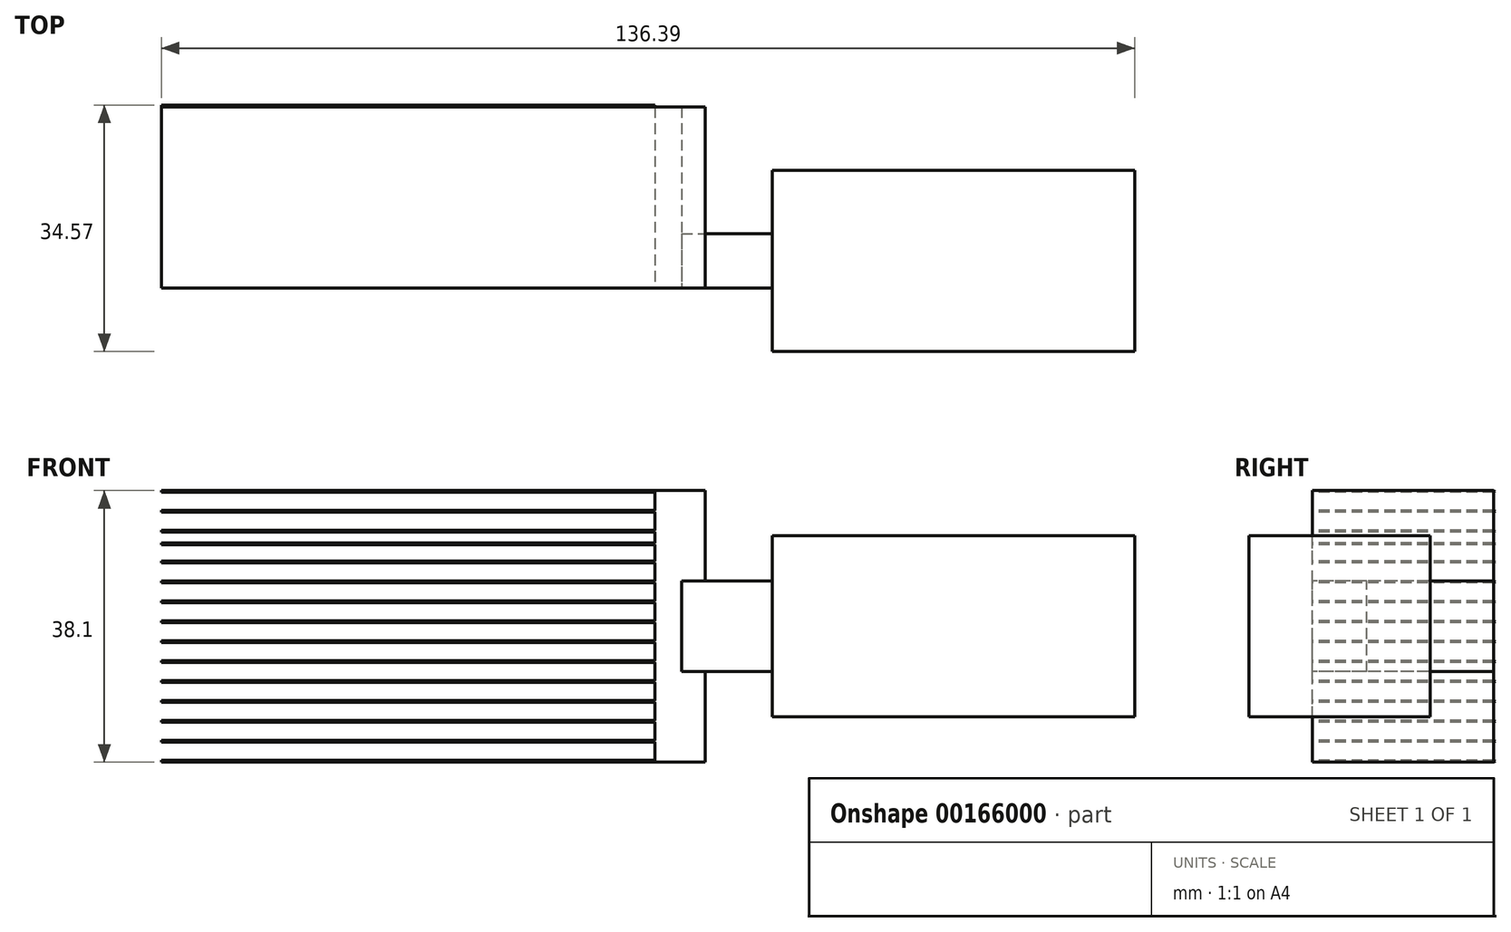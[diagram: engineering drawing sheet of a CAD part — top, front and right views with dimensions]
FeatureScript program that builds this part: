
annotation { "Feature Type Name" : "Feature", "Feature Type Description" : "" }
export const myFeature = defineFeature(function(context is Context, id is Id, definition is map)
    precondition{}
    {
        {
            var Q0;
            Q0=qCreatedBy(makeId("Front.planeOp"),FACE);
            var sketch = newSketch(context, id + "F0", { "sketchPlane" : qUnion([Q0])});
            skLineSegment(sketch, "E0.bottom", {"start": v(0, 0) * mm, "end": v(50.8, 0) * mm});
            skLineSegment(sketch, "E0.top", {"start": v(0, 25.4) * mm, "end": v(50.8, 25.4) * mm});
            skLineSegment(sketch, "E0.left", {"start": v(0, 0) * mm, "end": v(0, 25.4) * mm});
            skLineSegment(sketch, "E0.right", {"start": v(50.8, 0) * mm, "end": v(50.8, 25.4) * mm});
            skSolve(sketch);
        }
        {
            var Q0;
            Q0=makeQuery(id+"F0.imprint","IMPRINT",FACE,{"disambiguationData":[TD([[makeQuery(id+"F0.imprint","IMPRINT",EDGE,{"derivedFrom":sQuery(id+"F0.wireOp",EDGE,"E0.bottom")}),1.0]])]});
            extrude(context, id + "F1", {"entities" : qUnion([Q0]), "depth" : 25.4 * mm});
        }
        {
            var Q0;
            Q0=makeQuery(id+"F1.opExtrude","SWEPT_FACE",FACE,{"disambiguationData":[OSD([sQuery(id+"F0.wireOp",EDGE,"E0.left")])]});
            var sketch = newSketch(context, id + "F2", { "sketchPlane" : qUnion([Q0])});
            skLineSegment(sketch, "E1.0", {"start": v(8.9, 6.35) * mm, "end": v(16.51, 6.35) * mm});
            skLineSegment(sketch, "E2.0", {"start": v(8.9, 19.05) * mm, "end": v(16.51, 19.05) * mm});
            skLineSegment(sketch, "E3.0", {"start": v(16.51, 6.35) * mm, "end": v(16.51, 19.05) * mm});
            skLineSegment(sketch, "E4.0", {"start": v(8.9, 6.35) * mm, "end": v(8.9, 19.05) * mm});
            skPoint(sketch, "E5.orphan", {"position": v(0, 12.7) * mm});
            skPoint(sketch, "E6.orphan", {"position": v(12.7, 25.4) * mm});
            skPoint(sketch, "E7.orphan", {"position": v(25.4, 12.7) * mm});
            skPoint(sketch, "E8.orphan", {"position": v(12.7, 0) * mm});
            skSolve(sketch);
        }
        {
            var Q0;
            Q0 = qSketchRegion(id + "F2", true);
            extrude(context, id + "F3", {"entities" : qUnion([Q0]), "operationType" : NewBodyOperationType.ADD, "depth" : 12.7 * mm});
        }
        {
            var Q0;
            Q0=makeQuery(id+"F3.opExtrude","SWEPT_FACE",FACE,{"disambiguationData":[OSD([sQuery(id+"F2.wireOp",EDGE,"E3.0")])]});
            var sketch = newSketch(context, id + "F4", { "sketchPlane" : qUnion([Q0])});
            skLineSegment(sketch, "E9", {"start": v(-9.39, -6.35) * mm, "end": v(-9.39, 6.35) * mm});
            skLineSegment(sketch, "E10", {"start": v(-9.39, 19.05) * mm, "end": v(-12.7, 19.05) * mm});
            skLineSegment(sketch, "E11", {"start": v(-12.7, 19.05) * mm, "end": v(-12.7, 6.35) * mm});
            skLineSegment(sketch, "E12", {"start": v(-12.7, 6.35) * mm, "end": v(-9.39, 6.35) * mm});
            skLineSegment(sketch, "E13", {"start": v(-9.39, 19.05) * mm, "end": v(-9.39, 31.75) * mm});
            skLineSegment(sketch, "E14", {"start": v(-16.46, 31.75) * mm, "end": v(-85.59, 31.75) * mm});
            skLineSegment(sketch, "E15", {"start": v(-9.39, -6.35) * mm, "end": v(-85.59, -6.35) * mm});
            skLineSegment(sketch, "E16", {"start": v(-85.59, -6.35) * mm, "end": v(-85.59, -6.1) * mm});
            skLineSegment(sketch, "E17", {"start": v(-85.59, -6.1) * mm, "end": v(-16.46, -6.1) * mm});
            skLineSegment(sketch, "E18.0", {"start": v(-85.59, -3.56) * mm, "end": v(-16.46, -3.56) * mm});
            skLineSegment(sketch, "E19.0", {"start": v(-85.59, -3.3) * mm, "end": v(-16.46, -3.3) * mm});
            skLineSegment(sketch, "E20.0", {"start": v(-85.59, -0.76) * mm, "end": v(-16.46, -0.76) * mm});
            skLineSegment(sketch, "E21.0", {"start": v(-16.46, 31.5) * mm, "end": v(-85.59, 31.5) * mm});
            skLineSegment(sketch, "E22.0", {"start": v(-16.46, 28.96) * mm, "end": v(-85.59, 28.96) * mm});
            skLineSegment(sketch, "E23.0", {"start": v(-16.46, 28.7) * mm, "end": v(-85.59, 28.7) * mm});
            skLineSegment(sketch, "E24.0", {"start": v(-16.46, 26.16) * mm, "end": v(-85.59, 26.16) * mm});
            skLineSegment(sketch, "E25.0", {"start": v(-16.46, 25.9) * mm, "end": v(-85.59, 25.9) * mm});
            skLineSegment(sketch, "E26.0", {"start": v(-85.59, -0.5) * mm, "end": v(-16.46, -0.5) * mm});
            skLineSegment(sketch, "E27.0", {"start": v(-85.59, 2.03) * mm, "end": v(-16.46, 2.03) * mm});
            skLineSegment(sketch, "E28.0", {"start": v(-85.59, 2.29) * mm, "end": v(-16.46, 2.29) * mm});
            skLineSegment(sketch, "E29.0", {"start": v(-85.59, 4.83) * mm, "end": v(-16.46, 4.83) * mm});
            skLineSegment(sketch, "E30.0", {"start": v(-85.59, 5.08) * mm, "end": v(-16.46, 5.08) * mm});
            skLineSegment(sketch, "E31.0", {"start": v(-85.59, 7.62) * mm, "end": v(-16.46, 7.62) * mm});
            skLineSegment(sketch, "E32.0", {"start": v(-85.59, 7.87) * mm, "end": v(-16.46, 7.87) * mm});
            skLineSegment(sketch, "E33.0", {"start": v(-85.59, 10.41) * mm, "end": v(-16.46, 10.41) * mm});
            skLineSegment(sketch, "E34.0", {"start": v(-85.59, 10.67) * mm, "end": v(-16.46, 10.67) * mm});
            skLineSegment(sketch, "E35.0", {"start": v(-85.59, 13.2) * mm, "end": v(-16.46, 13.2) * mm});
            skLineSegment(sketch, "E36.0", {"start": v(-85.59, 13.46) * mm, "end": v(-16.46, 13.46) * mm});
            skLineSegment(sketch, "E37.0", {"start": v(-85.59, 16) * mm, "end": v(-16.46, 16) * mm});
            skLineSegment(sketch, "E38.0", {"start": v(-85.59, 16.26) * mm, "end": v(-16.46, 16.26) * mm});
            skLineSegment(sketch, "E39.0", {"start": v(-85.59, 18.8) * mm, "end": v(-16.46, 18.8) * mm});
            skLineSegment(sketch, "E40.0", {"start": v(-85.59, 19.05) * mm, "end": v(-16.46, 19.05) * mm});
            skLineSegment(sketch, "E41.0", {"start": v(-85.59, 21.59) * mm, "end": v(-16.46, 21.59) * mm});
            skLineSegment(sketch, "E42.0", {"start": v(-85.59, 21.84) * mm, "end": v(-16.46, 21.84) * mm});
            skLineSegment(sketch, "E43.0", {"start": v(-85.59, 24.38) * mm, "end": v(-16.46, 24.38) * mm});
            skLineSegment(sketch, "E44.0", {"start": v(-85.59, 24.13) * mm, "end": v(-16.46, 24.13) * mm});
            skLineSegment(sketch, "E45", {"start": v(-16.46, 31.75) * mm, "end": v(-9.39, 31.75) * mm});
            skLineSegment(sketch, "E46", {"start": v(-16.46, -6.1) * mm, "end": v(-16.46, -3.56) * mm});
            skLineSegment(sketch, "E47.trimOffspring", {"start": v(-16.46, 21.84) * mm, "end": v(-16.46, 24.13) * mm});
            skLineSegment(sketch, "E48.trimOffspring", {"start": v(-16.46, 19.05) * mm, "end": v(-16.46, 21.59) * mm});
            skLineSegment(sketch, "E49.trimOffspring", {"start": v(-16.46, 16.26) * mm, "end": v(-16.46, 18.8) * mm});
            skLineSegment(sketch, "E50.trimOffspring", {"start": v(-16.46, 13.46) * mm, "end": v(-16.46, 16) * mm});
            skLineSegment(sketch, "E51.trimOffspring", {"start": v(-16.46, 10.67) * mm, "end": v(-16.46, 13.2) * mm});
            skLineSegment(sketch, "E52.trimOffspring", {"start": v(-16.46, 7.87) * mm, "end": v(-16.46, 10.41) * mm});
            skLineSegment(sketch, "E53.trimOffspring", {"start": v(-16.46, 5.08) * mm, "end": v(-16.46, 7.62) * mm});
            skLineSegment(sketch, "E54.trimOffspring", {"start": v(-16.46, 2.29) * mm, "end": v(-16.46, 4.83) * mm});
            skLineSegment(sketch, "E55.trimOffspring", {"start": v(-16.46, -0.5) * mm, "end": v(-16.46, 2.03) * mm});
            skLineSegment(sketch, "E56.trimOffspring", {"start": v(-16.46, -3.3) * mm, "end": v(-16.46, -0.76) * mm});
            skPoint(sketch, "E57.orphan", {"position": v(-16.46, -6.35) * mm});
            skLineSegment(sketch, "E58", {"start": v(-85.59, -3.56) * mm, "end": v(-85.59, -3.3) * mm});
            skLineSegment(sketch, "E59.trimOffspring", {"start": v(-85.59, 31.5) * mm, "end": v(-85.59, 31.75) * mm});
            skLineSegment(sketch, "E60.trimOffspring", {"start": v(-85.59, 28.7) * mm, "end": v(-85.59, 28.96) * mm});
            skLineSegment(sketch, "E61.trimOffspring", {"start": v(-85.59, 25.9) * mm, "end": v(-85.59, 26.16) * mm});
            skLineSegment(sketch, "E62.trimOffspring", {"start": v(-85.59, 24.13) * mm, "end": v(-85.59, 24.38) * mm});
            skLineSegment(sketch, "E63.trimOffspring", {"start": v(-85.59, 21.59) * mm, "end": v(-85.59, 21.84) * mm});
            skLineSegment(sketch, "E64.trimOffspring", {"start": v(-85.59, 18.8) * mm, "end": v(-85.59, 19.05) * mm});
            skLineSegment(sketch, "E65.trimOffspring", {"start": v(-85.59, 16) * mm, "end": v(-85.59, 16.26) * mm});
            skLineSegment(sketch, "E66.trimOffspring", {"start": v(-85.59, 13.2) * mm, "end": v(-85.59, 13.46) * mm});
            skLineSegment(sketch, "E67.trimOffspring", {"start": v(-85.59, 10.41) * mm, "end": v(-85.59, 10.67) * mm});
            skLineSegment(sketch, "E68.trimOffspring", {"start": v(-85.59, 7.62) * mm, "end": v(-85.59, 7.87) * mm});
            skLineSegment(sketch, "E69.trimOffspring", {"start": v(-85.59, 4.83) * mm, "end": v(-85.59, 5.08) * mm});
            skLineSegment(sketch, "E70.trimOffspring", {"start": v(-85.59, 2.03) * mm, "end": v(-85.59, 2.29) * mm});
            skLineSegment(sketch, "E71.trimOffspring", {"start": v(-85.59, -0.76) * mm, "end": v(-85.59, -0.5) * mm});
            skLineSegment(sketch, "E72", {"start": v(-16.46, 24.38) * mm, "end": v(-16.46, 25.9) * mm});
            skLineSegment(sketch, "E73", {"start": v(-16.46, 26.16) * mm, "end": v(-16.46, 28.7) * mm});
            skLineSegment(sketch, "E74", {"start": v(-16.46, 28.96) * mm, "end": v(-16.46, 31.5) * mm});
            skSolve(sketch);
        }
        {
            var Q0;
            Q0 = qSketchRegion(id + "F4", true);
            extrude(context, id + "F5", {"entities" : qUnion([Q0]), "oppositeDirection" : true, "depth" : 25.4 * mm});
        }
        {
            var Q0;
            Q0=makeQuery(id+"F5.opExtrude","SWEPT_FACE",FACE,{"disambiguationData":[OSD([sQuery(id+"F4.wireOp",EDGE,"E59.trimOffspring")])]});
            var sketch = newSketch(context, id + "F6", { "sketchPlane" : qUnion([Q0])});
            skLineSegment(sketch, "E75", {"start": v(-8.89, 31.75) * mm, "end": v(-9.11, 31.62) * mm});
            skPoint(sketch, "E75.endSnap0", {"position": v(-8.89, 31.62) * mm});
            skLineSegment(sketch, "E76", {"start": v(-9.11, 31.62) * mm, "end": v(-8.89, 31.5) * mm});
            skSolve(sketch);
        }
        {
            var Q0;
            Q0=makeQuery(id+"F6.imprint","IMPRINT",FACE,{"disambiguationData":[TD([[makeQuery(id+"F6.imprint","IMPRINT",EDGE,{"derivedFrom":sQuery(id+"F6.wireOp",EDGE,"E75")}),1.0]])]});
            extrude(context, id + "F7", {"entities" : qUnion([Q0]), "operationType" : NewBodyOperationType.ADD, "oppositeDirection" : true, "depth" : 69.12 * mm});
        }
        {
            var Q0;
            Q0=makeQuery(id+"F5.opExtrude","SWEPT_FACE",FACE,{"disambiguationData":[OSD([sQuery(id+"F4.wireOp",EDGE,"E60.trimOffspring")])]});
            var sketch = newSketch(context, id + "F8", { "sketchPlane" : qUnion([Q0])});
            skLineSegment(sketch, "E77", {"start": v(-8.89, 28.96) * mm, "end": v(-9.12, 28.83) * mm});
            skPoint(sketch, "E77.endSnap0", {"position": v(-8.89, 28.83) * mm});
            skLineSegment(sketch, "E78", {"start": v(-9.12, 28.83) * mm, "end": v(-8.89, 28.7) * mm});
            skSolve(sketch);
        }
        {
            var Q0;
            Q0=makeQuery(id+"F5.opExtrude","SWEPT_FACE",FACE,{"disambiguationData":[OSD([sQuery(id+"F4.wireOp",EDGE,"E61.trimOffspring")])]});
            var sketch = newSketch(context, id + "F9", { "sketchPlane" : qUnion([Q0])});
            skLineSegment(sketch, "E79", {"start": v(-8.89, 26.16) * mm, "end": v(-9.1, 26.04) * mm});
            skPoint(sketch, "E79.endSnap0", {"position": v(-8.89, 26.04) * mm});
            skLineSegment(sketch, "E80", {"start": v(-9.1, 26.04) * mm, "end": v(-8.89, 25.9) * mm});
            skSolve(sketch);
        }
        {
            var Q0;
            Q0=makeQuery(id+"F5.opExtrude","SWEPT_FACE",FACE,{"disambiguationData":[OSD([sQuery(id+"F4.wireOp",EDGE,"E62.trimOffspring")])]});
            var sketch = newSketch(context, id + "F10", { "sketchPlane" : qUnion([Q0])});
            skLineSegment(sketch, "E81", {"start": v(-8.89, 24.38) * mm, "end": v(-9.11, 24.26) * mm});
            skPoint(sketch, "E81.endSnap0", {"position": v(-8.89, 24.26) * mm});
            skLineSegment(sketch, "E82", {"start": v(-9.11, 24.26) * mm, "end": v(-8.89, 24.13) * mm});
            skSolve(sketch);
        }
        {
            var Q0;
            Q0=makeQuery(id+"F5.opExtrude","SWEPT_FACE",FACE,{"disambiguationData":[OSD([sQuery(id+"F4.wireOp",EDGE,"E63.trimOffspring")])]});
            var sketch = newSketch(context, id + "F11", { "sketchPlane" : qUnion([Q0])});
            skLineSegment(sketch, "E83", {"start": v(-8.89, 21.84) * mm, "end": v(-9.1, 21.72) * mm});
            skPoint(sketch, "E83.endSnap0", {"position": v(-8.89, 21.72) * mm});
            skLineSegment(sketch, "E84", {"start": v(-9.1, 21.72) * mm, "end": v(-8.89, 21.59) * mm});
            skSolve(sketch);
        }
        {
            var Q0;
            Q0=makeQuery(id+"F5.opExtrude","SWEPT_FACE",FACE,{"disambiguationData":[OSD([sQuery(id+"F4.wireOp",EDGE,"E64.trimOffspring")])]});
            var sketch = newSketch(context, id + "F12", { "sketchPlane" : qUnion([Q0])});
            skLineSegment(sketch, "E85", {"start": v(-8.89, 19.05) * mm, "end": v(-9.14, 18.92) * mm});
            skPoint(sketch, "E85.endSnap0", {"position": v(-8.89, 18.92) * mm});
            skLineSegment(sketch, "E86", {"start": v(-9.14, 18.92) * mm, "end": v(-8.89, 18.8) * mm});
            skSolve(sketch);
        }
        {
            var Q0;
            Q0=makeQuery(id+"F5.opExtrude","SWEPT_FACE",FACE,{"disambiguationData":[OSD([sQuery(id+"F4.wireOp",EDGE,"E65.trimOffspring")])]});
            var sketch = newSketch(context, id + "F13", { "sketchPlane" : qUnion([Q0])});
            skLineSegment(sketch, "E87", {"start": v(-8.89, 16.26) * mm, "end": v(-9.1, 16.13) * mm});
            skPoint(sketch, "E87.endSnap0", {"position": v(-8.89, 16.13) * mm});
            skLineSegment(sketch, "E88", {"start": v(-9.1, 16.13) * mm, "end": v(-8.89, 16) * mm});
            skSolve(sketch);
        }
        {
            var Q0;
            Q0=makeQuery(id+"F5.opExtrude","SWEPT_FACE",FACE,{"disambiguationData":[OSD([sQuery(id+"F4.wireOp",EDGE,"E66.trimOffspring")])]});
            var sketch = newSketch(context, id + "F14", { "sketchPlane" : qUnion([Q0])});
            skLineSegment(sketch, "E89", {"start": v(-8.89, 13.46) * mm, "end": v(-9.17, 13.33) * mm});
            skPoint(sketch, "E89.endSnap0", {"position": v(-8.89, 13.33) * mm});
            skLineSegment(sketch, "E90", {"start": v(-9.17, 13.33) * mm, "end": v(-8.89, 13.2) * mm});
            skSolve(sketch);
        }
        {
            var Q0;
            Q0=makeQuery(id+"F5.opExtrude","SWEPT_FACE",FACE,{"disambiguationData":[OSD([sQuery(id+"F4.wireOp",EDGE,"E67.trimOffspring")])]});
            var sketch = newSketch(context, id + "F15", { "sketchPlane" : qUnion([Q0])});
            skLineSegment(sketch, "E91", {"start": v(-8.89, 10.67) * mm, "end": v(-9.14, 10.54) * mm});
            skPoint(sketch, "E91.endSnap0", {"position": v(-8.89, 10.54) * mm});
            skLineSegment(sketch, "E92", {"start": v(-9.14, 10.54) * mm, "end": v(-8.89, 10.41) * mm});
            skSolve(sketch);
        }
        {
            var Q0;
            Q0=makeQuery(id+"F5.opExtrude","SWEPT_FACE",FACE,{"disambiguationData":[OSD([sQuery(id+"F4.wireOp",EDGE,"E68.trimOffspring")])]});
            var sketch = newSketch(context, id + "F16", { "sketchPlane" : qUnion([Q0])});
            skLineSegment(sketch, "E93", {"start": v(-8.89, 7.87) * mm, "end": v(-9.16, 7.75) * mm});
            skPoint(sketch, "E93.endSnap0", {"position": v(-8.89, 7.75) * mm});
            skLineSegment(sketch, "E94", {"start": v(-9.16, 7.75) * mm, "end": v(-8.89, 7.62) * mm});
            skSolve(sketch);
        }
        {
            var Q0;
            Q0=makeQuery(id+"F5.opExtrude","SWEPT_FACE",FACE,{"disambiguationData":[OSD([sQuery(id+"F4.wireOp",EDGE,"E69.trimOffspring")])]});
            var sketch = newSketch(context, id + "F17", { "sketchPlane" : qUnion([Q0])});
            skLineSegment(sketch, "E95", {"start": v(-8.89, 5.08) * mm, "end": v(-9.13, 4.95) * mm});
            skPoint(sketch, "E95.endSnap0", {"position": v(-8.89, 4.95) * mm});
            skLineSegment(sketch, "E96", {"start": v(-9.13, 4.95) * mm, "end": v(-8.89, 4.83) * mm});
            skSolve(sketch);
        }
        {
            var Q0;
            Q0=makeQuery(id+"F5.opExtrude","SWEPT_FACE",FACE,{"disambiguationData":[OSD([sQuery(id+"F4.wireOp",EDGE,"E70.trimOffspring")])]});
            var sketch = newSketch(context, id + "F18", { "sketchPlane" : qUnion([Q0])});
            skLineSegment(sketch, "E97", {"start": v(-8.89, 2.29) * mm, "end": v(-9.12, 2.16) * mm});
            skPoint(sketch, "E97.endSnap0", {"position": v(-8.89, 2.16) * mm});
            skLineSegment(sketch, "E98", {"start": v(-9.12, 2.16) * mm, "end": v(-8.89, 2.03) * mm});
            skSolve(sketch);
        }
        {
            var Q0;
            Q0=makeQuery(id+"F5.opExtrude","SWEPT_FACE",FACE,{"disambiguationData":[OSD([sQuery(id+"F4.wireOp",EDGE,"E71.trimOffspring")])]});
            var sketch = newSketch(context, id + "F19", { "sketchPlane" : qUnion([Q0])});
            skLineSegment(sketch, "E99", {"start": v(-8.89, -0.5) * mm, "end": v(-9.16, -0.64) * mm});
            skPoint(sketch, "E99.endSnap0", {"position": v(-8.89, -0.64) * mm});
            skLineSegment(sketch, "E100", {"start": v(-9.16, -0.64) * mm, "end": v(-8.89, -0.76) * mm});
            skSolve(sketch);
        }
        {
            var Q0;
            Q0=makeQuery(id+"F5.opExtrude","SWEPT_FACE",FACE,{"disambiguationData":[OSD([sQuery(id+"F4.wireOp",EDGE,"E58")])]});
            var sketch = newSketch(context, id + "F20", { "sketchPlane" : qUnion([Q0])});
            skLineSegment(sketch, "E101", {"start": v(-8.89, -3.3) * mm, "end": v(-9.14, -3.43) * mm});
            skPoint(sketch, "E101.endSnap0", {"position": v(-8.89, -3.43) * mm});
            skLineSegment(sketch, "E102", {"start": v(-9.14, -3.43) * mm, "end": v(-8.89, -3.56) * mm});
            skSolve(sketch);
        }
        {
            var Q0;
            Q0=makeQuery(id+"F5.opExtrude","SWEPT_FACE",FACE,{"disambiguationData":[OSD([sQuery(id+"F4.wireOp",EDGE,"E16")])]});
            var sketch = newSketch(context, id + "F21", { "sketchPlane" : qUnion([Q0])});
            skLineSegment(sketch, "E103", {"start": v(-8.89, -6.1) * mm, "end": v(-9.12, -6.22) * mm});
            skPoint(sketch, "E103.endSnap0", {"position": v(-8.89, -6.22) * mm});
            skLineSegment(sketch, "E104", {"start": v(-9.12, -6.22) * mm, "end": v(-8.89, -6.35) * mm});
            skSolve(sketch);
        }
        {
            var Q0;
            Q0=makeQuery(id+"F8.imprint","IMPRINT",FACE,{"disambiguationData":[TD([[makeQuery(id+"F8.imprint","IMPRINT",EDGE,{"derivedFrom":sQuery(id+"F8.wireOp",EDGE,"E77")}),1.0]])]});
            extrude(context, id + "F22", {"entities" : qUnion([Q0]), "operationType" : NewBodyOperationType.ADD, "oppositeDirection" : true, "depth" : 69.12 * mm});
        }
        {
            var Q0;
            Q0=makeQuery(id+"F9.imprint","IMPRINT",FACE,{"disambiguationData":[TD([[makeQuery(id+"F9.imprint","IMPRINT",EDGE,{"derivedFrom":sQuery(id+"F9.wireOp",EDGE,"E79")}),1.0]])]});
            extrude(context, id + "F23", {"entities" : qUnion([Q0]), "oppositeDirection" : true, "depth" : 69.12 * mm});
        }
        {
            var Q0;
            Q0=makeQuery(id+"F10.imprint","IMPRINT",FACE,{"disambiguationData":[TD([[makeQuery(id+"F10.imprint","IMPRINT",EDGE,{"derivedFrom":sQuery(id+"F10.wireOp",EDGE,"E81")}),1.0]])]});
            extrude(context, id + "F24", {"entities" : qUnion([Q0]), "oppositeDirection" : true, "depth" : 69.12 * mm});
        }
        {
            var Q0;
            Q0=makeQuery(id+"F11.imprint","IMPRINT",FACE,{"disambiguationData":[TD([[makeQuery(id+"F11.imprint","IMPRINT",EDGE,{"derivedFrom":sQuery(id+"F11.wireOp",EDGE,"E83")}),1.0]])]});
            extrude(context, id + "F25", {"entities" : qUnion([Q0]), "oppositeDirection" : true, "depth" : 69.12 * mm});
        }
        {
            var Q0;
            Q0=makeQuery(id+"F12.imprint","IMPRINT",FACE,{"disambiguationData":[TD([[makeQuery(id+"F12.imprint","IMPRINT",EDGE,{"derivedFrom":sQuery(id+"F12.wireOp",EDGE,"E85")}),1.0]])]});
            extrude(context, id + "F26", {"entities" : qUnion([Q0]), "oppositeDirection" : true, "depth" : 69.12 * mm});
        }
        {
            var Q0;
            Q0=makeQuery(id+"F13.imprint","IMPRINT",FACE,{"disambiguationData":[TD([[makeQuery(id+"F13.imprint","IMPRINT",EDGE,{"derivedFrom":sQuery(id+"F13.wireOp",EDGE,"E87")}),1.0]])]});
            extrude(context, id + "F27", {"entities" : qUnion([Q0]), "oppositeDirection" : true, "depth" : 69.12 * mm});
        }
        {
            var Q0;
            Q0=makeQuery(id+"F14.imprint","IMPRINT",FACE,{"disambiguationData":[TD([[makeQuery(id+"F14.imprint","IMPRINT",EDGE,{"derivedFrom":sQuery(id+"F14.wireOp",EDGE,"E89")}),1.0]])]});
            extrude(context, id + "F28", {"entities" : qUnion([Q0]), "oppositeDirection" : true, "depth" : 69.12 * mm});
        }
        {
            var Q0;
            Q0=makeQuery(id+"F15.imprint","IMPRINT",FACE,{"disambiguationData":[TD([[makeQuery(id+"F15.imprint","IMPRINT",EDGE,{"derivedFrom":sQuery(id+"F15.wireOp",EDGE,"E91")}),1.0]])]});
            extrude(context, id + "F29", {"entities" : qUnion([Q0]), "oppositeDirection" : true, "depth" : 69.12 * mm});
        }
        {
            var Q0;
            Q0=makeQuery(id+"F16.imprint","IMPRINT",FACE,{"disambiguationData":[TD([[makeQuery(id+"F16.imprint","IMPRINT",EDGE,{"derivedFrom":sQuery(id+"F16.wireOp",EDGE,"E93")}),1.0]])]});
            extrude(context, id + "F30", {"entities" : qUnion([Q0]), "operationType" : NewBodyOperationType.ADD, "oppositeDirection" : true, "depth" : 69.12 * mm});
        }
        {
            var Q0;
            Q0=makeQuery(id+"F17.imprint","IMPRINT",FACE,{"disambiguationData":[TD([[makeQuery(id+"F17.imprint","IMPRINT",EDGE,{"derivedFrom":sQuery(id+"F17.wireOp",EDGE,"E95")}),1.0]])]});
            extrude(context, id + "F31", {"entities" : qUnion([Q0]), "operationType" : NewBodyOperationType.ADD, "oppositeDirection" : true, "depth" : 69.12 * mm});
        }
        {
            var Q0;
            Q0=makeQuery(id+"F18.imprint","IMPRINT",FACE,{"disambiguationData":[TD([[makeQuery(id+"F18.imprint","IMPRINT",EDGE,{"derivedFrom":sQuery(id+"F18.wireOp",EDGE,"E97")}),1.0]])]});
            extrude(context, id + "F32", {"entities" : qUnion([Q0]), "oppositeDirection" : true, "depth" : 69.12 * mm});
        }
        {
            var Q0;
            Q0=makeQuery(id+"F19.imprint","IMPRINT",FACE,{"disambiguationData":[TD([[makeQuery(id+"F19.imprint","IMPRINT",EDGE,{"derivedFrom":sQuery(id+"F19.wireOp",EDGE,"E99")}),1.0]])]});
            extrude(context, id + "F33", {"entities" : qUnion([Q0]), "operationType" : NewBodyOperationType.ADD, "oppositeDirection" : true, "depth" : 69.12 * mm});
        }
        {
            var Q0;
            Q0=makeQuery(id+"F20.imprint","IMPRINT",FACE,{"disambiguationData":[TD([[makeQuery(id+"F20.imprint","IMPRINT",EDGE,{"derivedFrom":sQuery(id+"F20.wireOp",EDGE,"E101")}),1.0]])]});
            extrude(context, id + "F34", {"entities" : qUnion([Q0]), "operationType" : NewBodyOperationType.ADD, "oppositeDirection" : true, "depth" : 69.12 * mm});
        }
        {
            var Q0;
            Q0=makeQuery(id+"F21.imprint","IMPRINT",FACE,{"disambiguationData":[TD([[makeQuery(id+"F21.imprint","IMPRINT",EDGE,{"derivedFrom":sQuery(id+"F21.wireOp",EDGE,"E103")}),1.0]])]});
            extrude(context, id + "F35", {"entities" : qUnion([Q0]), "operationType" : NewBodyOperationType.ADD, "oppositeDirection" : true, "depth" : 69.12 * mm});
        }
    });
